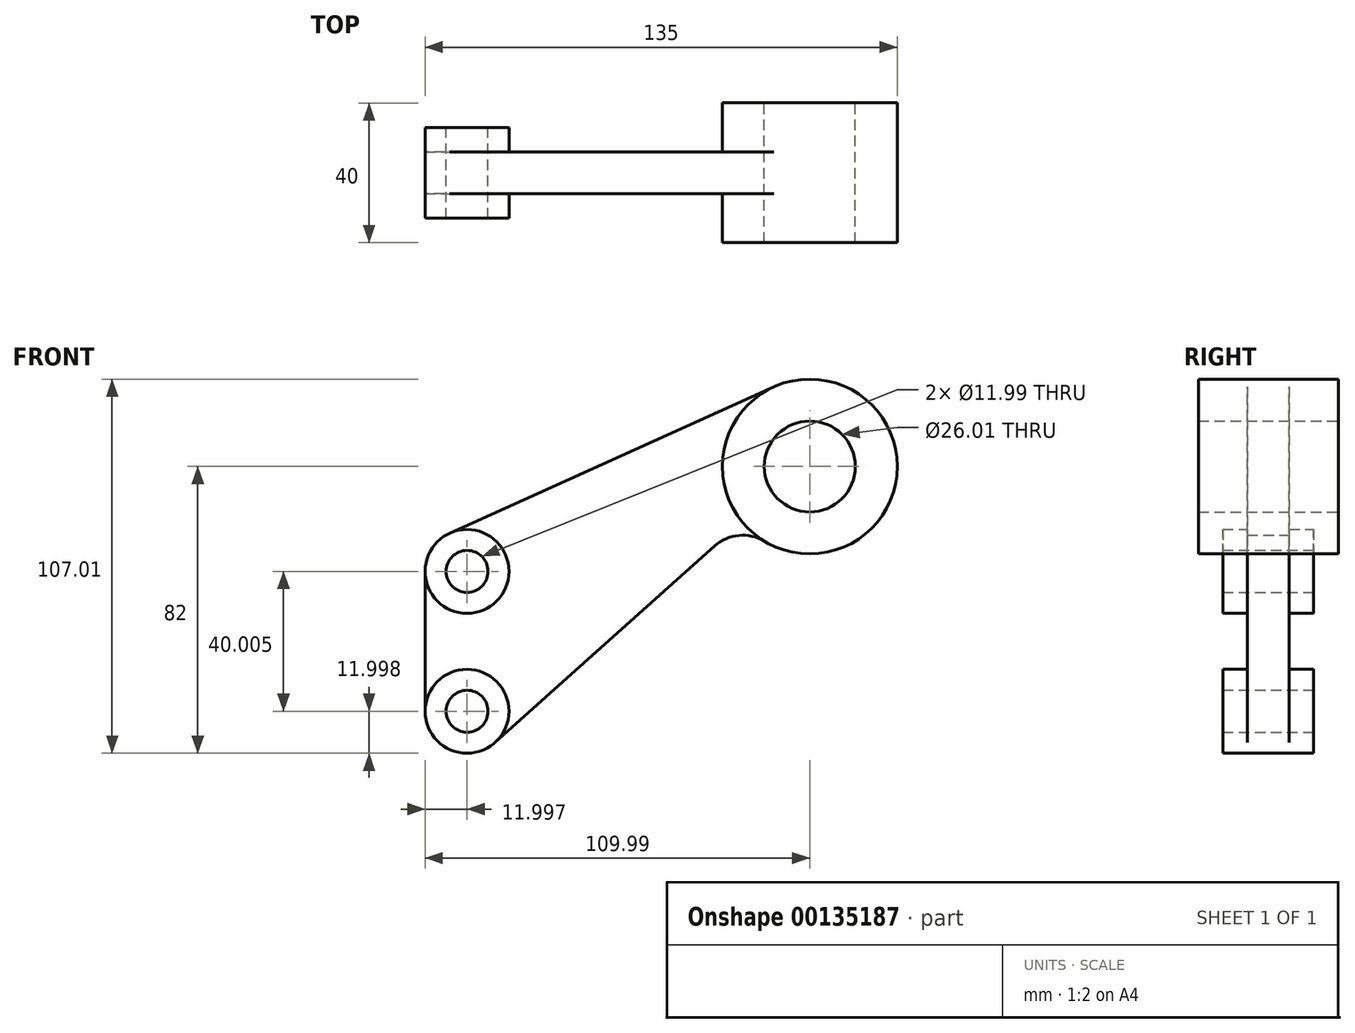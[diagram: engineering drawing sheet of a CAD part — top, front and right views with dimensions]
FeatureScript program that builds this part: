
annotation { "Feature Type Name" : "Feature", "Feature Type Description" : "" }
export const myFeature = defineFeature(function(context is Context, id is Id, definition is map)
    precondition{}
    {
        {
            var Q0;
            Q0=qCreatedBy(makeId("Front.planeOp"),FACE);
            var sketch = newSketch(context, id + "F0", { "sketchPlane" : qUnion([Q0])});
            skCircle(sketch, "E0", {"center": v(0, 0) * mm, "radius": 25 * mm});
            skCircle(sketch, "E1", {"center": v(0, 0) * mm, "radius": 13 * mm});
            skCircle(sketch, "E2", {"center": v(-98, -30) * mm, "radius": 12 * mm});
            skCircle(sketch, "E3", {"center": v(-98, -30) * mm, "radius": 6 * mm});
            skCircle(sketch, "E4", {"center": v(-98, -70) * mm, "radius": 12 * mm});
            skCircle(sketch, "E5", {"center": v(-98, -70) * mm, "radius": 6 * mm});
            skLineSegment(sketch, "E6", {"start": v(-102.93, -19.06) * mm, "end": v(-10.3, 22.79) * mm});
            skLineSegment(sketch, "E7", {"start": v(-110, -30) * mm, "end": v(-110, -70) * mm});
            skArc(sketch, "E8", {"start": v(-12.95, -21.4) * mm, "mid": v(-20.27, -19.71) * mm, "end": v(-27.15, -22.71) * mm});
            skLineSegment(sketch, "E9", {"start": v(-90, -78.95) * mm, "end": v(-27.15, -22.71) * mm});
            skSolve(sketch);
        }
        {
            var Q0;
            Q0=makeQuery(id+"F0.imprint","IMPRINT",FACE,{"disambiguationData":[TD([[makeQuery(id+"F0.imprint","IMPRINT",EDGE,{"derivedFrom":sQuery(id+"F0.wireOp",EDGE,"E1")}),-1.0]])]});
            extrude(context, id + "F1", {"entities" : qUnion([Q0]), "endBound" : BoundingType.SYMMETRIC, "depth" : 40 * mm});
        }
        {
            var Q0;
            {var subQ0=sQuery(id+"F0.wireOp",EDGE,"E6");Q0=makeQuery(id+"F0.imprint","IMPRINT",FACE,{"disambiguationData":[TD([[makeQuery(id+"F0.imprint","IMPRINT",EDGE,{"derivedFrom":subQ0}),-1.0]])]});}
            extrude(context, id + "F2", {"entities" : qUnion([Q0]), "operationType" : NewBodyOperationType.ADD, "endBound" : BoundingType.SYMMETRIC, "depth" : 12 * mm});
        }
        {
            var Q0;
            Q0=makeQuery(id+"F0.imprint","IMPRINT",FACE,{"disambiguationData":[TD([[makeQuery(id+"F0.imprint","IMPRINT",EDGE,{"derivedFrom":sQuery(id+"F0.wireOp",EDGE,"E3")}),-1.0]])]});
            var Q1;
            Q1=makeQuery(id+"F0.imprint","IMPRINT",FACE,{"disambiguationData":[TD([[makeQuery(id+"F0.imprint","IMPRINT",EDGE,{"derivedFrom":sQuery(id+"F0.wireOp",EDGE,"E5")}),-1.0]])]});
            extrude(context, id + "F3", {"entities" : qUnion([Q0, Q1]), "operationType" : NewBodyOperationType.ADD, "endBound" : BoundingType.SYMMETRIC, "depth" : 26 * mm});
        }
    });
